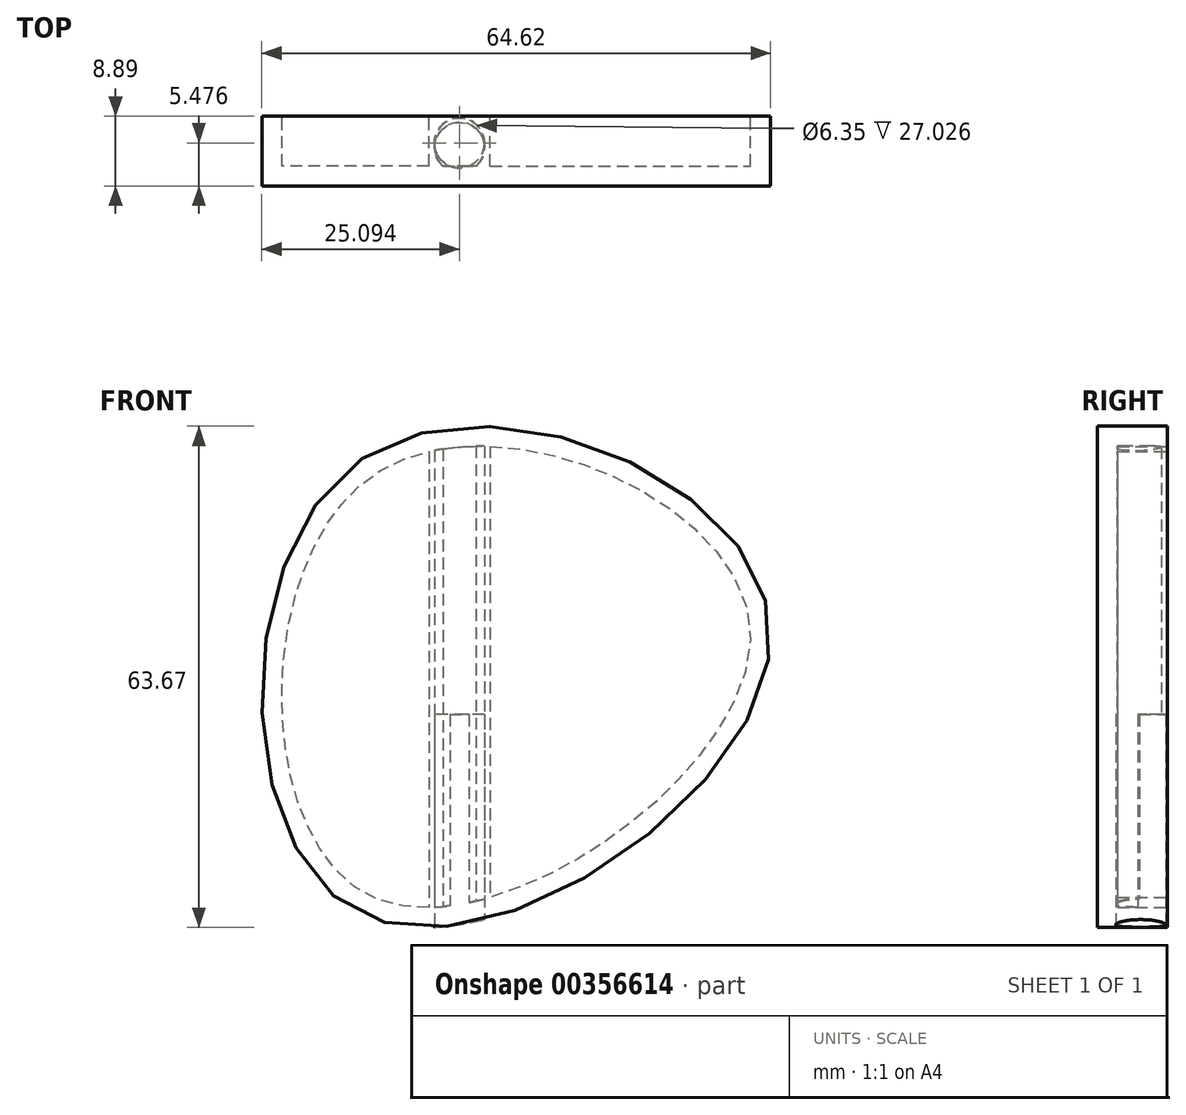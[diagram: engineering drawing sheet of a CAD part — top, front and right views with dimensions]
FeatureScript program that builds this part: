
annotation { "Feature Type Name" : "Feature", "Feature Type Description" : "" }
export const myFeature = defineFeature(function(context is Context, id is Id, definition is map)
    precondition{}
    {
        {
            var Q0;
            Q0=qCreatedBy(makeId("Front.planeOp"),FACE);
            var sketch = newSketch(context, id + "F0", { "sketchPlane" : qUnion([Q0])});
            skFitSpline(sketch, "E0", {"points": [v(0, 57.9) * mm, v(51.87, 36.39) * mm, v(0, 0) * mm, v(0, 57.9) * mm]});
            skSolve(sketch);
        }
        {
            var Q0;
            Q0 = qSketchRegion(id + "F0", true);
            extrude(context, id + "F1", {"entities" : qUnion([Q0]), "depth" : 8.9 * mm});
        }
        {
            var Q0;
            Q0=makeQuery(id+"F1.opExtrude","CAP_FACE",FACE,{"disambiguationData":[OSD([sQuery(id+"F0.wireOp",EDGE,"E0")])],"isStart":true});
            var Q1;
            Q1=makeQuery(id+"F1.opExtrude","SWEPT_BODY",BODY,{"disambiguationData":[OSD([sQuery(id+"F0.wireOp",EDGE,"E0")])]});
            shell(context, id + "F2", {"entities" : qUnion([Q0]), "parts" : qUnion([Q1]), "thickness" : 2.54 * mm});
        }
        {
            var Q0;
            Q0=qCreatedBy(makeId("Top.planeOp"),FACE);
            var sketch = newSketch(context, id + "F3", { "sketchPlane" : qUnion([Q0])});
            skLineSegment(sketch, "E1", {"start": v(8.51, -7.98) * mm, "end": v(8.51, 0) * mm});
            skLineSegment(sketch, "E2", {"start": v(16.27, -7.98) * mm, "end": v(16.27, 0) * mm});
            skLineSegment(sketch, "E3", {"start": v(16.27, 0) * mm, "end": v(8.51, 0) * mm});
            skLineSegment(sketch, "E4", {"start": v(8.51, -7.98) * mm, "end": v(16.27, -7.98) * mm});
            skCircle(sketch, "E5", {"center": v(12.4, -3.97) * mm, "radius": 3.18 * mm});
            skPoint(sketch, "E5.centerSnap0", {"position": v(12.4, -7.98) * mm});
            skSolve(sketch);
        }
        {
            var Q0;
            Q0 = qSketchRegion(id + "F3", true);
            extrude(context, id + "F4", {"entities" : qUnion([Q0]), "operationType" : NewBodyOperationType.ADD, "depth" : 60.45 * mm});
        }
        {
            var Q0;
            Q0=qCreatedBy(makeId("Top.planeOp"),FACE);
            var sketch = newSketch(context, id + "F5", { "sketchPlane" : qUnion([Q0])});
            skCircle(sketch, "E6", {"center": v(12.37, -3.41) * mm, "radius": 3.17 * mm});
            skSolve(sketch);
        }
        {
            var Q0;
            Q0 = qSketchRegion(id + "F5", true);
            extrude(context, id + "F6", {"entities" : qUnion([Q0]), "operationType" : NewBodyOperationType.REMOVE, "depth" : 25.4 * mm});
        }
        {
            var Q0;
            Q0 = qSketchRegion(id + "F5", true);
            extrude(context, id + "F7", {"entities" : qUnion([Q0]), "operationType" : NewBodyOperationType.REMOVE, "oppositeDirection" : true, "depth" : 25.4 * mm});
        }
    });
